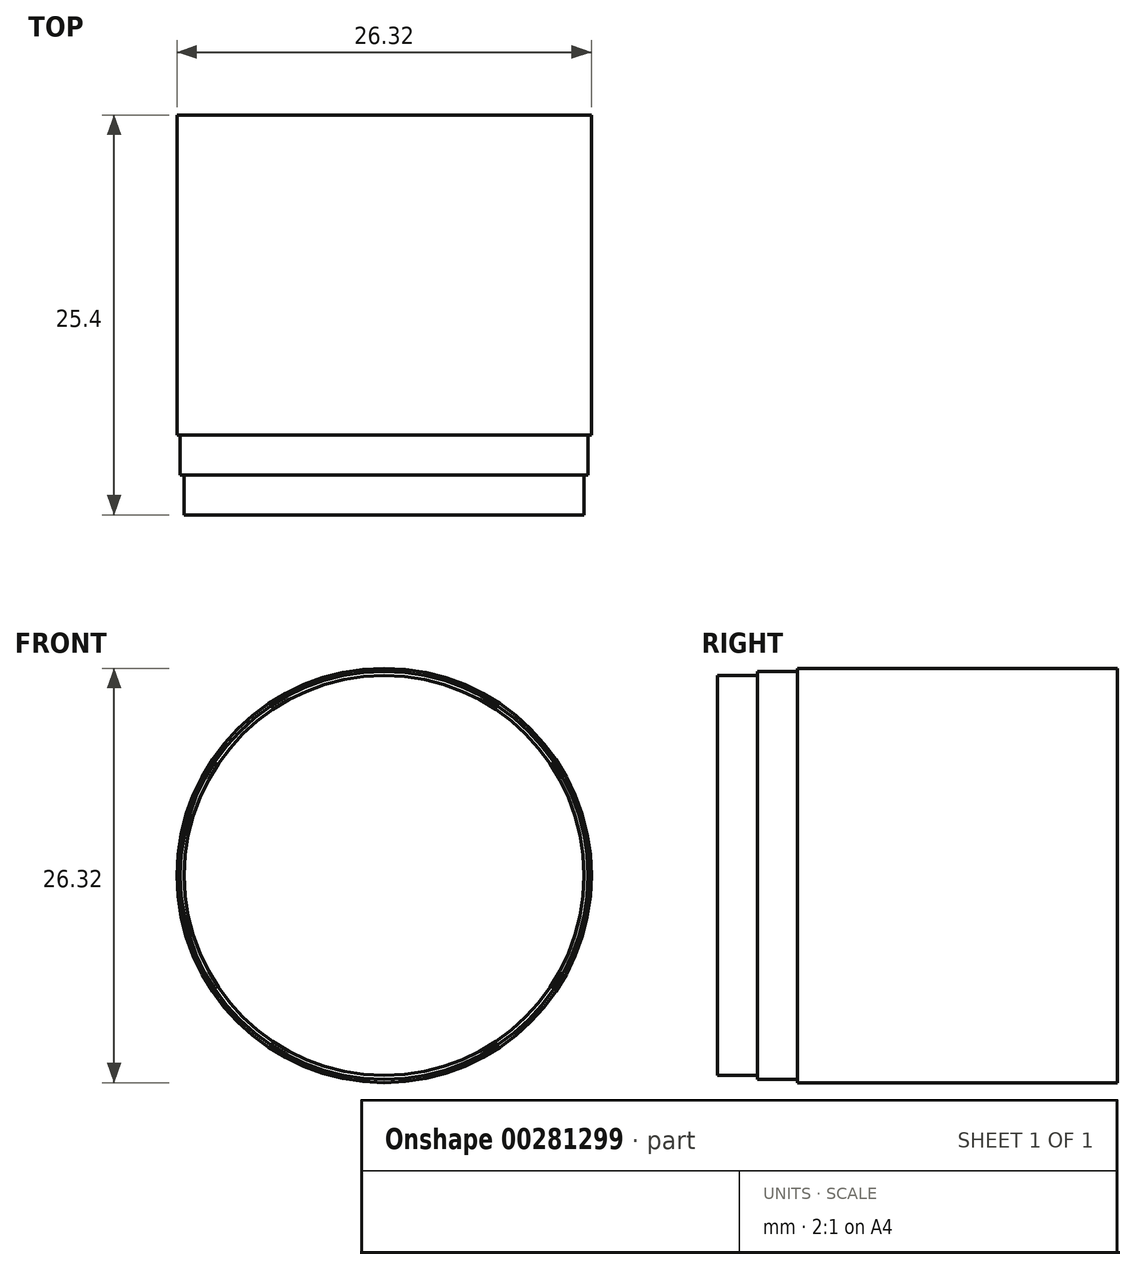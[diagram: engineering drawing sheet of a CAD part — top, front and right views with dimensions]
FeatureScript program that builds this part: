
annotation { "Feature Type Name" : "Feature", "Feature Type Description" : "" }
export const myFeature = defineFeature(function(context is Context, id is Id, definition is map)
    precondition{}
    {
        {
            var Q0;
            Q0=qCreatedBy(makeId("Front.planeOp"),FACE);
            var sketch = newSketch(context, id + "F0", { "sketchPlane" : qUnion([Q0])});
            skCircle(sketch, "E0", {"center": v(0, 0) * mm, "radius": 12.7 * mm});
            skSolve(sketch);
        }
        {
            var Q0;
            Q0 = qSketchRegion(id + "F0", true);
            extrude(context, id + "F1", {"entities" : qUnion([Q0]), "depth" : 25.4 * mm});
        }
        {
            var Q0;
            Q0=qCreatedBy(makeId("Front.planeOp"),FACE);
            var sketch = newSketch(context, id + "F2", { "sketchPlane" : qUnion([Q0])});
            skCircle(sketch, "E1", {"center": v(0, 0) * mm, "radius": 12.95 * mm});
            skSolve(sketch);
        }
        {
            var Q0;
            Q0 = qSketchRegion(id + "F2", true);
            extrude(context, id + "F3", {"entities" : qUnion([Q0]), "operationType" : NewBodyOperationType.ADD, "depth" : 22.86 * mm});
        }
        {
            var Q0;
            Q0=qCreatedBy(makeId("Front.planeOp"),FACE);
            var sketch = newSketch(context, id + "F4", { "sketchPlane" : qUnion([Q0])});
            skCircle(sketch, "E2", {"center": v(0, 0) * mm, "radius": 13.16 * mm});
            skSolve(sketch);
        }
        {
            var Q0;
            Q0 = qSketchRegion(id + "F4", true);
            extrude(context, id + "F5", {"entities" : qUnion([Q0]), "operationType" : NewBodyOperationType.ADD, "depth" : 20.32 * mm});
        }
    });
